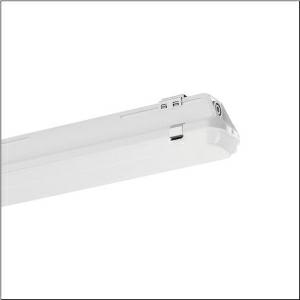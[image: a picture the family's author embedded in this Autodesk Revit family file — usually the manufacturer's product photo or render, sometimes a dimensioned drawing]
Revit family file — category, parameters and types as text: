
# Revit family: monsun_r__21_emergency_51fb10dp437b3h_9196
name_source: partatom
category: Lighting Fixtures
units: mm (PartAtom-declared; Revit-internal decimal feet)

## family parameters
Cut with Voids When Loaded = No
Host = Face
Light Source = No
Part Type = Normal
Room Calculation Point = No
Round Connector Dimension = Use Diameter
Shared = No

## types (1)
- --- (1 x LED, 3860 lm, 27.5 W, 4000K)
    Apparent Load = 28 VA
    CIE Flux Codes = 47 77 93 94 100
    Color Rendering = 80
    Color Temperature = 4000K
    Default Elevation = 1800 mm
    Description = Monsun® 21 emergency, damp-proof luminaire, chain hanger, primary optical cover: enclosure, of PMMA, light emission: direct distribution, primary light characteristic: symmetric, installation type: vertical mounting, horizontal mounting, surface-mounted, suspended mounting, LED, rated luminous flux: 3.860lm, luminous efficacy: 140lm/W, light colour: 840, colour temperature: 4000K, control gear: ECG DALI, with terminal, 5+3-pole, max. 2.5mm², mains connection: 220..240V, AC, 50/60Hz, rated input power: 28W, control gear: single battery element, battery: NiCd, 4,5Ah, mains connection: 230V, housing, of glass-fibre reinforced polyester, uncoated, bright grey, length: 1.590mm, width: 90mm, height: 88mm, clip for enclosure, of stainless steel (V2A), ceiling mounting element, of stainless steel (V2A), chain hanger, of stainless steel (V2A), protection rating (complete): IP66, insulation class (complete): insulation class I (protective earthing), certification: CE, UKCA, protection symbol: D, impact resistance: IK04, permissible operating ambient temperature: +5..+25°C, standard: EN 60598-2-1, EN 50419, EN 60598-2-22, corresponds to IFS (International Featured Standards) requirements for safety and quality in the food industry, for indoor or canopied outdoor use, no direct snow, no direct sun, no direct rain, packaging unit: 1 piece
    Height = 89 mm
    Lamp = 1 x LED
    Lamp Light Flux = 3860 lm
    Lamp Power = 27.5 W
    Lamp count = 1
    Length = 1590 mm
    Luminous efficacy = 140 lm/W
    Manufacturer = Siteco
    ModVariant = No
    Model = 51FB10DP437B3H
    Mounting Place = Ceiling
    Mounting Type = Pendant
    Number of Poles = 1
    OnlyDefault = Yes
    Power Factor = 1
    Product Name = Monsun® 21 emergency
    Product group = damp-proof luminaire | ceiling pendant
    ProductGroupID = 908
    Protection Class = Protection class I
    Protection Degree = IP 66
    RLX_Detail_Level = 1
    RlxData = <blob elided: 92093 chars, md5=c30957c0>
    Socket = socket
    Standby Power = 0 W
    System Light Flux = 3860 lm
    System Power = 28 W
    Type Comments = factory setting: luminous flux: 100 % | dim-lin: 254 | 162 mA
    Type Image = l_1006717.jpg
    URL = http://relux.com
    VarID = @adj_124915
    Voltage = 0 V
    Weight = 0.00 kg
    Width = 90 mm

## geometry (parser evidence)
native form markers: Blend x4, Sweep x14
no freeform markers — native parametric forms only
